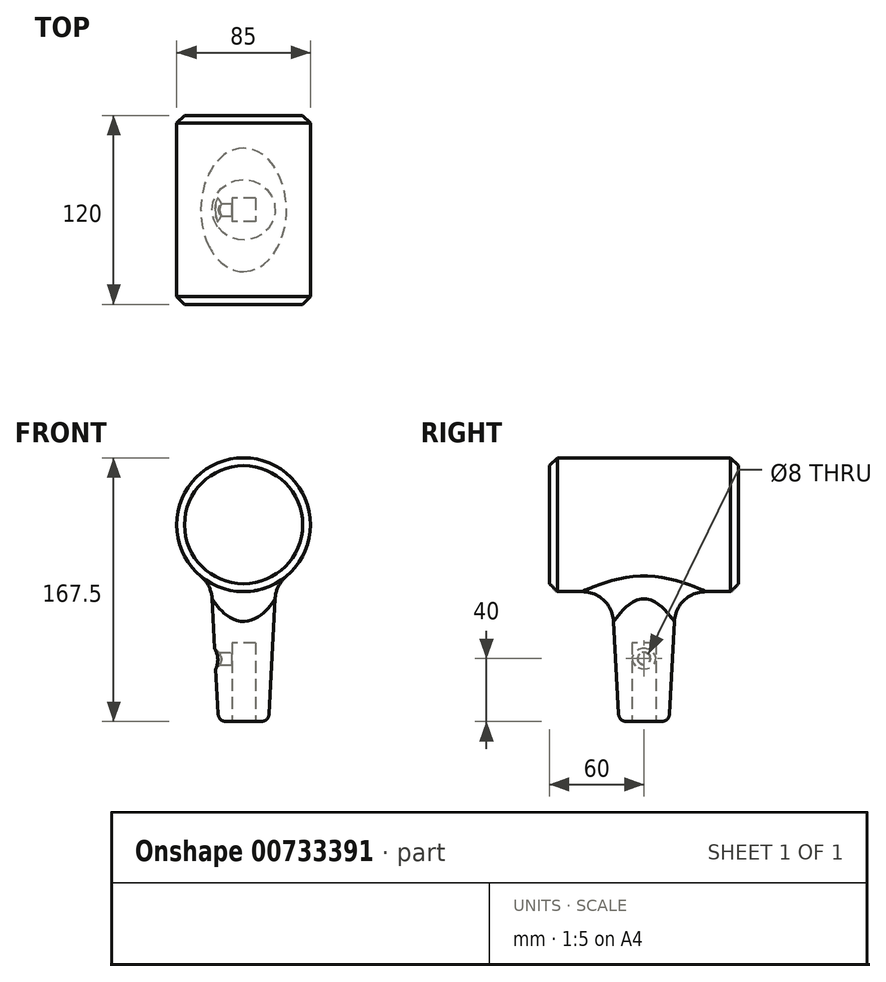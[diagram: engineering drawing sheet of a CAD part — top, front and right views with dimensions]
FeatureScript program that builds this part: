
annotation { "Feature Type Name" : "Feature", "Feature Type Description" : "" }
export const myFeature = defineFeature(function(context is Context, id is Id, definition is map)
    precondition{}
    {
        {
            var Q0;
            Q0=qCreatedBy(makeId("Front.planeOp"),FACE);
            var sketch = newSketch(context, id + "F0", { "sketchPlane" : qUnion([Q0])});
            skCircle(sketch, "E0", {"center": v(0, 0) * mm, "radius": 42.5 * mm});
            skSolve(sketch);
        }
        {
            var Q0;
            Q0=makeQuery(id+"F0.imprint","IMPRINT",FACE,{"disambiguationData":[TD([[makeQuery(id+"F0.imprint","IMPRINT",EDGE,{"derivedFrom":sQuery(id+"F0.wireOp",EDGE,"E0")}),1.0]])]});
            extrude(context, id + "F1", {"entities" : qUnion([Q0]), "endBound" : BoundingType.SYMMETRIC, "depth" : 120 * mm, "offsetDistance" : 25 * mm});
        }
        {
            var Q0;
            Q0=qCreatedBy(makeId("Top.planeOp"),FACE);
            var sketch = newSketch(context, id + "F2", { "sketchPlane" : qUnion([Q0])});
            skCircle(sketch, "E1", {"center": v(0, 0) * mm, "radius": 22.5 * mm});
            skSolve(sketch);
        }
        {
            var Q0;
            Q0 = qSketchRegion(id + "F2", true);
            extrude(context, id + "F3", {"entities" : qUnion([Q0]), "operationType" : NewBodyOperationType.ADD, "oppositeDirection" : true, "depth" : 125 * mm, "offsetDistance" : 25 * mm, "hasDraft" : true, "draftAngle" : 3 * degree, "draftPullDirection" : true});
        }
        {
            var Q0;
            Q0=makeQuery(id+"F3.opExtrude","CAP_FACE",FACE,{"disambiguationData":[OSD([sQuery(id+"F2.wireOp",EDGE,"E1")])],"isStart":false});
            var sketch = newSketch(context, id + "F4", { "sketchPlane" : qUnion([Q0])});
            skPoint(sketch, "E2.middle", {"position": v(0, 0) * mm});
            skLineSegment(sketch, "E3.bottom", {"start": v(7.5, -7.5) * mm, "end": v(-7.5, -7.5) * mm});
            skLineSegment(sketch, "E3.top", {"start": v(7.5, 7.5) * mm, "end": v(-7.5, 7.5) * mm});
            skLineSegment(sketch, "E3.left", {"start": v(7.5, -7.5) * mm, "end": v(7.5, 7.5) * mm});
            skLineSegment(sketch, "E3.right", {"start": v(-7.5, -7.5) * mm, "end": v(-7.5, 7.5) * mm});
            skSolve(sketch);
        }
        {
            var Q0;
            Q0=makeQuery(id+"F4.imprint","IMPRINT",FACE,{"disambiguationData":[TD([[makeQuery(id+"F4.imprint","IMPRINT",EDGE,{"derivedFrom":sQuery(id+"F4.wireOp",EDGE,"E3.bottom")}),-1.0]])]});
            var Q1;
            Q1 = qSketchRegion(id + "F4", true);
            extrude(context, id + "F5", {"entities" : qUnion([Q0, Q1]), "operationType" : NewBodyOperationType.REMOVE, "oppositeDirection" : true, "depth" : 50 * mm, "offsetDistance" : 25 * mm});
        }
        {
            var Q0;
            Q0=qCreatedBy(makeId("Right.planeOp"),FACE);
            var sketch = newSketch(context, id + "F6", { "sketchPlane" : qUnion([Q0])});
            skCircle(sketch, "E4", {"center": v(0, -85) * mm, "radius": 4 * mm});
            skSolve(sketch);
        }
        {
            var Q0;
            Q0 = qSketchRegion(id + "F6", true);
            extrude(context, id + "F7", {"entities" : qUnion([Q0]), "operationType" : NewBodyOperationType.REMOVE, "oppositeDirection" : true, "depth" : 25 * mm, "offsetDistance" : 25 * mm});
        }
        {
            var Q0;
            Q0=makeQuery(id+"F1.opExtrude","CAP_FACE",FACE,{"disambiguationData":[OSD([sQuery(id+"F0.wireOp",EDGE,"E0")])],"isStart":false});
            var Q1;
            Q1=makeQuery(id+"F1.opExtrude","CAP_FACE",FACE,{"disambiguationData":[OSD([sQuery(id+"F0.wireOp",EDGE,"E0")])],"isStart":true});
            chamfer(context, id + "F8", {"entities" : qUnion([Q0, Q1]), "width" : 5 * mm, "tangentPropagation" : true});
        }
        {
            var Q0;
            Q0=makeQuery(id+"F3.boolean.opBoolean","INTERSECT",EDGE,{"derivedFrom":[makeQuery(id+"F1.opExtrude","SWEPT_FACE",FACE,{"disambiguationData":[OSD([sQuery(id+"F0.wireOp",EDGE,"E0")])]}),makeQuery(id+"F3.opExtrude","SWEPT_FACE",FACE,{"disambiguationData":[OSD([sQuery(id+"F2.wireOp",EDGE,"E1")])]})]});
            fillet(context, id + "F9", {"entities" : qUnion([Q0]), "radius" : 20 * mm, "tangentPropagation" : true, "allowEdgeOverflow" : false});
        }
        {
            var Q0;
            Q0=makeQuery(id+"F3.opExtrude","CAP_EDGE",EDGE,{"disambiguationData":[OSD([sQuery(id+"F2.wireOp",EDGE,"E1")])],"isStart":false});
            fillet(context, id + "F10", {"entities" : qUnion([Q0]), "radius" : 5 * mm, "tangentPropagation" : true, "allowEdgeOverflow" : false});
        }
        {
            var Q0;
            Q0=makeQuery(id+"F7.boolean.opBoolean","INTERSECT",EDGE,{"derivedFrom":[makeQuery(id+"F3.opExtrude","SWEPT_FACE",FACE,{"disambiguationData":[OSD([sQuery(id+"F2.wireOp",EDGE,"E1")])]}),makeQuery(id+"F7.opExtrude","SWEPT_FACE",FACE,{"disambiguationData":[OSD([sQuery(id+"F6.wireOp",EDGE,"E4")])]})]});
            chamfer(context, id + "F11", {"entities" : qUnion([Q0]), "width" : 2.5 * mm, "tangentPropagation" : true});
        }
    });
